# Revit family: C9400
name_source: partatom
category: Specialty Equipment
units: mm (PartAtom-declared; Revit-internal decimal feet)

## family parameters
Always vertical = Yes
Cut with Voids When Loaded = No
Maintain Annotation Orientation = No
Part Type = Normal
Room Calculation Point = No
Round Connector Dimension = Use Diameter
Shared = No
Work Plane-Based = No

## types (1)
- C9400 Sinks
    Cold Water Maximum Pressure = 125.00 psi
    Cold Water Minimum Pressure = 20.00 psi
    Default Elevation = 0' - 0"
    Depth = 0' - 5"
    Description = Hand Sink
    Height = 0' - 10"
    Hot Water Maximum Pressure = 125.00 psi
    Hot Water Minimum Pressure = 20.00 psi
    Indirect Waste Size = 2"
    Length = 1' - 2"
    Manufacturer = Krome Usa Inc.
    Material = Stainless Steel
    Maximum Temperature = 140 °F
    Minimum Teperature = 40 °F
    Model = C9400
    Plumbing Remarks = Discharge Rate: 18.00 GPM Max
    Product Name = Stainless Steel Deck Mount Commercial Kitchen Sink 14"X10"
    URL = https://www.aluids.com

## geometry (parser evidence)
native form markers: Sweep x2
no freeform markers — native parametric forms only
